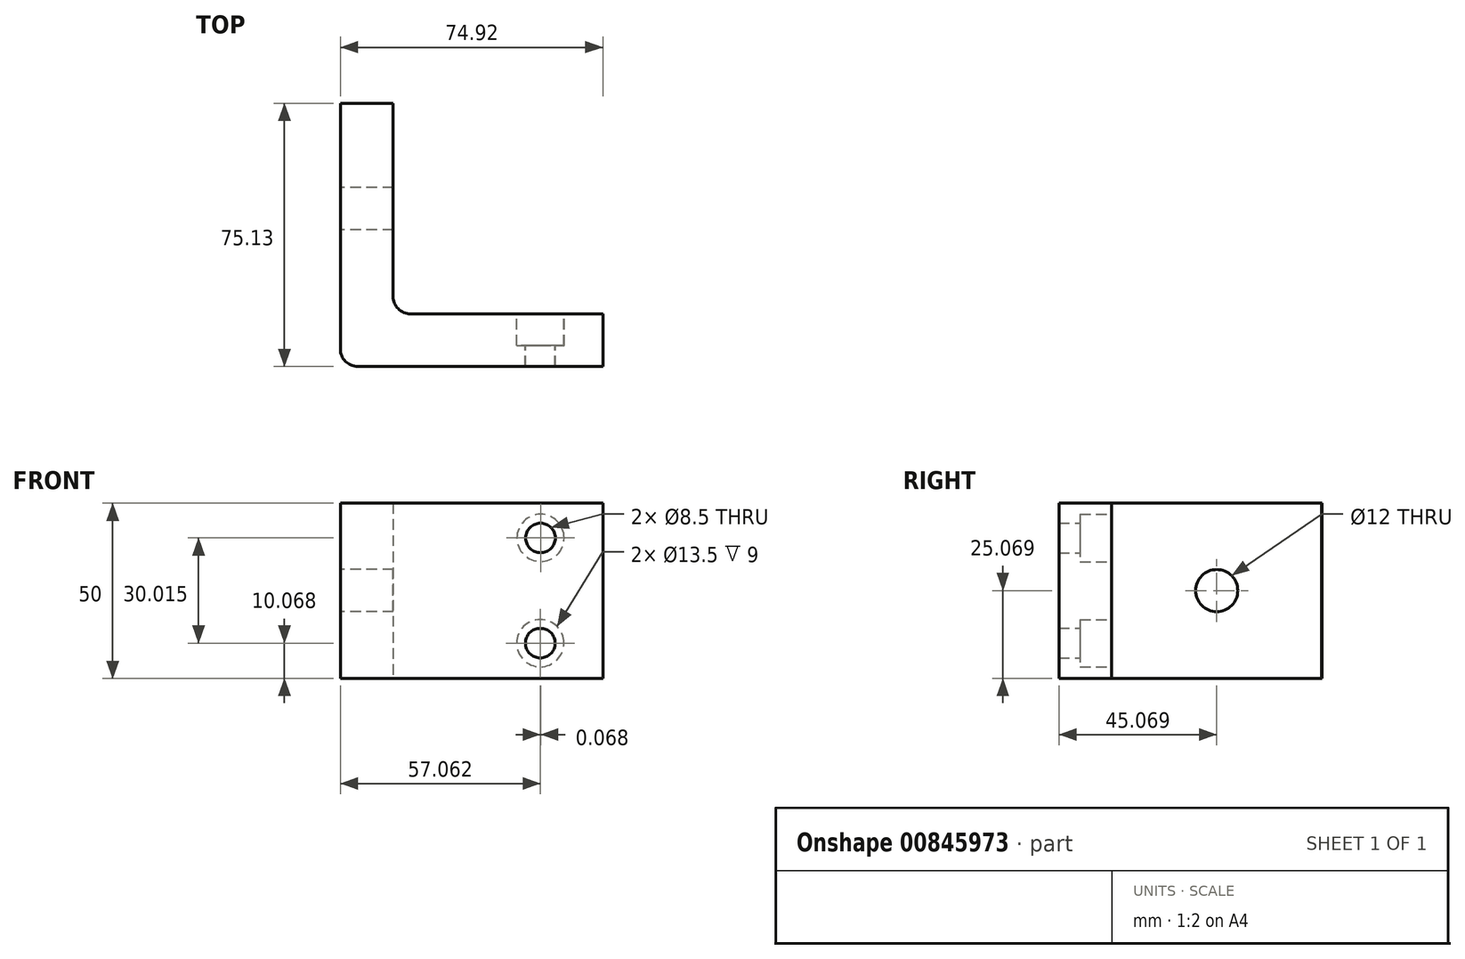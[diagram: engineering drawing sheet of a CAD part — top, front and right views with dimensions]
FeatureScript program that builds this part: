
annotation { "Feature Type Name" : "Feature", "Feature Type Description" : "" }
export const myFeature = defineFeature(function(context is Context, id is Id, definition is map)
    precondition{}
    {
        {
            var Q0;
            Q0=qCreatedBy(makeId("Top.planeOp"),FACE);
            var sketch = newSketch(context, id + "F0", { "sketchPlane" : qUnion([Q0])});
            skLineSegment(sketch, "E0.left", {"start": v(0, 5) * mm, "end": v(0, 75.13) * mm});
            skLineSegment(sketch, "E1", {"start": v(15.04, 75.03) * mm, "end": v(0, 75.13) * mm});
            skPoint(sketch, "E2.visualSharp", {"position": v(0, 0) * mm});
            skArc(sketch, "E2.filletArc", {"start": v(0, 5) * mm, "mid": v(1.46, 1.46) * mm, "end": v(5, 0) * mm});
            skLineSegment(sketch, "E3.left", {"start": v(15.04, 75.03) * mm, "end": v(15.04, 25.04) * mm});
            skLineSegment(sketch, "E4.top", {"start": v(20.04, 15.01) * mm, "end": v(74.92, 15.01) * mm});
            skLineSegment(sketch, "E4.left", {"start": v(15.04, 75.03) * mm, "end": v(15.04, 20.01) * mm});
            skPoint(sketch, "E5.visualSharp", {"position": v(15.04, 15.01) * mm});
            skArc(sketch, "E5.filletArc", {"start": v(15.04, 20.01) * mm, "mid": v(16.5, 16.48) * mm, "end": v(20.04, 15.01) * mm});
            skLineSegment(sketch, "E6", {"start": v(74.92, 15.01) * mm, "end": v(74.92, 0) * mm});
            skLineSegment(sketch, "E7", {"start": v(5, 0) * mm, "end": v(74.92, 0) * mm});
            skLineSegment(sketch, "E8.left", {"start": v(74.92, 15.01) * mm, "end": v(74.92, 15.01) * mm});
            skLineSegment(sketch, "E8.right", {"start": v(56.9, 15.01) * mm, "end": v(56.9, 15.01) * mm});
            skLineSegment(sketch, "E9.left", {"start": v(50.15, 15.01) * mm, "end": v(50.15, 6.06) * mm});
            skLineSegment(sketch, "E9.right", {"start": v(63.61, 15.01) * mm, "end": v(63.61, 6.06) * mm});
            skLineSegment(sketch, "E10.bottom", {"start": v(56.88, 0) * mm, "end": v(61.09, 0) * mm});
            skLineSegment(sketch, "E11", {"start": v(61.09, 0) * mm, "end": v(61.09, 6.06) * mm});
            skLineSegment(sketch, "E12", {"start": v(63.61, 6.06) * mm, "end": v(61.09, 6.06) * mm});
            skLineSegment(sketch, "E13", {"start": v(50.15, 6.06) * mm, "end": v(52.67, 6.06) * mm});
            skLineSegment(sketch, "E14", {"start": v(52.67, 6.06) * mm, "end": v(52.67, 0) * mm});
            skLineSegment(sketch, "E15.bottom", {"start": v(15.04, 75.03) * mm, "end": v(0, 75.03) * mm});
            skLineSegment(sketch, "E15.left", {"start": v(15.04, 75.03) * mm, "end": v(15.04, 45.06) * mm});
            skLineSegment(sketch, "E15.right", {"start": v(0, 75.03) * mm, "end": v(0, 45.06) * mm});
            skLineSegment(sketch, "E16.top", {"start": v(0, 51.04) * mm, "end": v(15.04, 51.04) * mm});
            skLineSegment(sketch, "E17.top", {"start": v(0, 39.04) * mm, "end": v(15.04, 39.04) * mm});
            skSolve(sketch);
        }
        {
            var Q0;
            Q0 = qSketchRegion(id + "F0", true);
            extrude(context, id + "F1", {"entities" : qUnion([Q0]), "depth" : 50 * mm, "offsetDistance" : 25 * mm});
        }
        {
            var Q0;
            Q0=qCreatedBy(makeId("Right.planeOp"),FACE);
            var sketch = newSketch(context, id + "F2", { "sketchPlane" : qUnion([Q0])});
            skLineSegment(sketch, "E18.bottom", {"start": v(0, 0) * mm, "end": v(75.06, 0) * mm});
            skLineSegment(sketch, "E18.top", {"start": v(0, 50.04) * mm, "end": v(75.06, 50.04) * mm});
            skLineSegment(sketch, "E18.left", {"start": v(0, 0) * mm, "end": v(0, 50.04) * mm});
            skLineSegment(sketch, "E18.right", {"start": v(75.06, 0) * mm, "end": v(75.06, 50.04) * mm});
            skLineSegment(sketch, "E19.bottom", {"start": v(75.06, 50.04) * mm, "end": v(45.07, 50.04) * mm});
            skLineSegment(sketch, "E19.top", {"start": v(75.06, 25.07) * mm, "end": v(45.07, 25.07) * mm});
            skLineSegment(sketch, "E19.left", {"start": v(75.06, 50.04) * mm, "end": v(75.06, 25.07) * mm});
            skLineSegment(sketch, "E19.right", {"start": v(45.07, 50.04) * mm, "end": v(45.07, 25.07) * mm});
            skSolve(sketch);
        }
        {
            var Q0;
            Q0=sQuery(id+"F2.wireOp",VERTEX,"E19.top.end");
            var Q1;
            Q1=makeQuery(id+"F1.opExtrude","SWEPT_BODY",BODY,{"disambiguationData":[OSD([sQuery(id+"F0.wireOp",EDGE,"E0.left"),sQuery(id+"F0.wireOp",EDGE,"E1"),sQuery(id+"F0.wireOp",EDGE,"E2.filletArc"),sQuery(id+"F0.wireOp",EDGE,"E4.top"),sQuery(id+"F0.wireOp",EDGE,"E4.left"),sQuery(id+"F0.wireOp",EDGE,"E5.filletArc"),sQuery(id+"F0.wireOp",EDGE,"E7"),sQuery(id+"F0.wireOp",EDGE,"E6"),sQuery(id+"F0.wireOp",EDGE,"E10.bottom"),sQuery(id+"F0.wireOp",EDGE,"E15.left"),sQuery(id+"F0.wireOp",EDGE,"E15.right")])]});
            hole(context, id + "F3", {"style" : HoleStyle.SIMPLE, "endStyle" : HoleEndStyle.THROUGH, "oppositeDirection" : true, "holeDiameter" : 12 * mm, "majorDiameter" : 5 * mm, "isTappedThrough" : true, "tappedDepth" : 12 * mm, "tapClearance" : 3, "locations" : qUnion([Q0]), "scope" : qUnion([Q1])});
        }
        {
            var Q0;
            Q0=makeQuery(id+"F1.opExtrude","SWEPT_FACE",FACE,{"disambiguationData":[OSD([sQuery(id+"F0.wireOp",EDGE,"E4.top")])]});
            var sketch = newSketch(context, id + "F4", { "sketchPlane" : qUnion([Q0])});
            skCircle(sketch, "E20", {"center": v(-57.13, 40.08) * mm, "radius": 4.25 * mm});
            skCircle(sketch, "E21", {"center": v(-57.06, 10.07) * mm, "radius": 4.24 * mm});
            skSolve(sketch);
        }
        {
            var Q0;
            Q0=sQuery(id+"F4.wireOp",VERTEX,"E20.center");
            var Q1;
            Q1=sQuery(id+"F4.wireOp",VERTEX,"E21.center");
            var Q2;
            Q2=makeQuery(id+"F1.opExtrude","SWEPT_BODY",BODY,{"disambiguationData":[OSD([sQuery(id+"F0.wireOp",EDGE,"E0.left"),sQuery(id+"F0.wireOp",EDGE,"E1"),sQuery(id+"F0.wireOp",EDGE,"E2.filletArc"),sQuery(id+"F0.wireOp",EDGE,"E4.top"),sQuery(id+"F0.wireOp",EDGE,"E4.left"),sQuery(id+"F0.wireOp",EDGE,"E5.filletArc"),sQuery(id+"F0.wireOp",EDGE,"E7"),sQuery(id+"F0.wireOp",EDGE,"E6"),sQuery(id+"F0.wireOp",EDGE,"E10.bottom"),sQuery(id+"F0.wireOp",EDGE,"E15.left"),sQuery(id+"F0.wireOp",EDGE,"E15.right")])]});
            hole(context, id + "F5", {"style" : HoleStyle.C_BORE, "endStyle" : HoleEndStyle.BLIND, "holeDiameter" : 8.5 * mm, "cBoreDiameter" : 13.5 * mm, "cBoreDepth" : 9 * mm, "majorDiameter" : 5 * mm, "holeDepth" : 15 * mm, "isTappedThrough" : true, "tappedDepth" : 12 * mm, "tapClearance" : 3, "locations" : qUnion([Q0, Q1]), "scope" : qUnion([Q2])});
        }
    });
